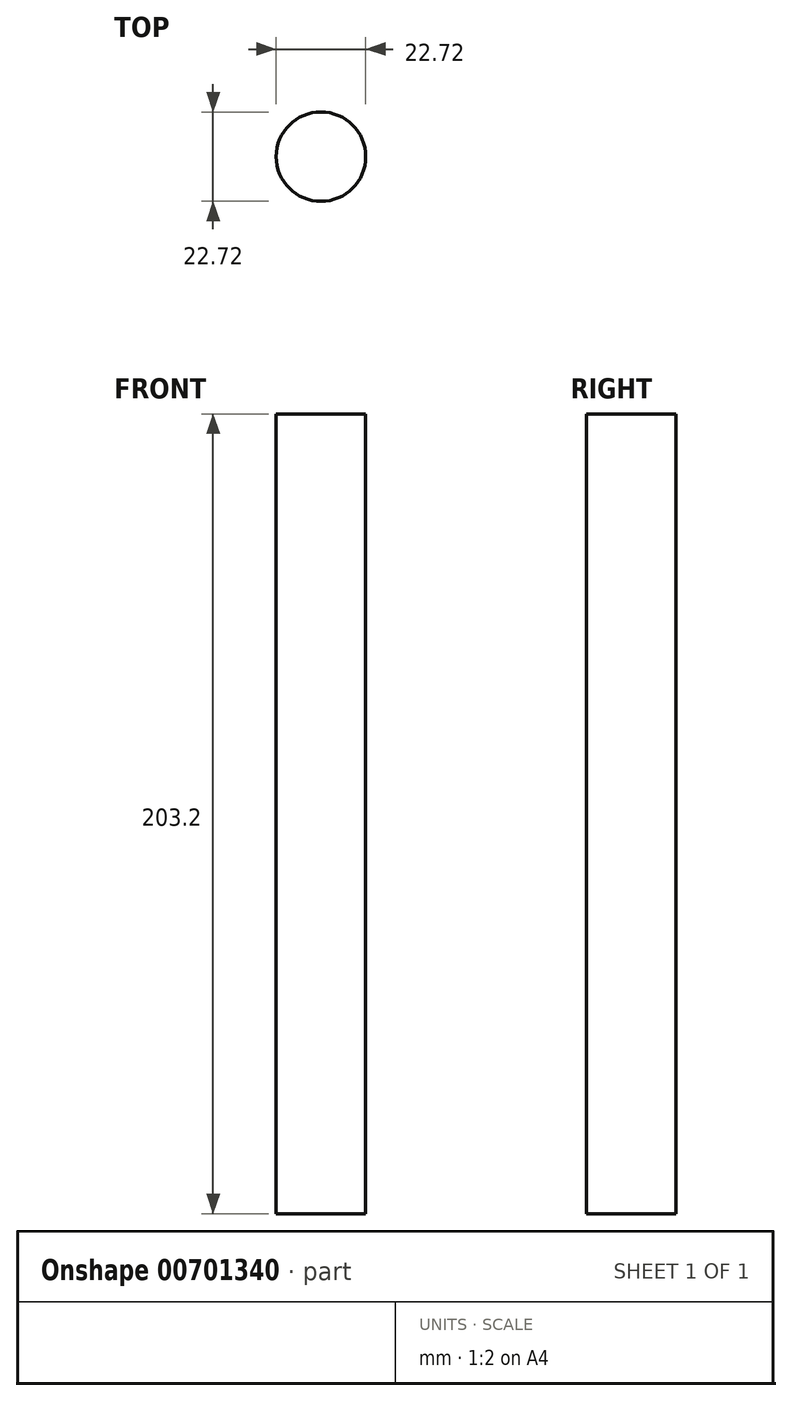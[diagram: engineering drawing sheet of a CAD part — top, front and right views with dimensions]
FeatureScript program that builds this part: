
annotation { "Feature Type Name" : "Feature", "Feature Type Description" : "" }
export const myFeature = defineFeature(function(context is Context, id is Id, definition is map)
    precondition{}
    {
        {
            var Q0;
            Q0=qCreatedBy(makeId("Top.planeOp"),FACE);
            var sketch = newSketch(context, id + "F0", { "sketchPlane" : qUnion([Q0])});
            skCircle(sketch, "E0", {"center": v(0, 0) * mm, "radius": 11.36 * mm});
            skSolve(sketch);
        }
        {
            var Q0;
            Q0=makeQuery(id+"F0.imprint","IMPRINT",FACE,{"disambiguationData":[TD([[makeQuery(id+"F0.imprint","IMPRINT",EDGE,{"derivedFrom":sQuery(id+"F0.wireOp",EDGE,"E0")}),1.0]])]});
            extrude(context, id + "F1", {"entities" : qUnion([Q0]), "depth" : 203.2 * mm, "offsetDistance" : 25.4 * mm});
        }
    });
